# Revit family: IS_Mara_A9009_BIM_NL
name_source: partatom
category: Plumbing Fixtures
revit_build: Autodesk Revit MEP 2014 (Build: 20130308_1515(x64)
units: mm (PartAtom-declared; Revit-internal decimal feet)

## types (1)
- A9009AA - MARA WASTAFELMENGKRAAN HOOG ZONDER WASTE
    AreaUnits = millimeters
    Assembly Code = C1030200
    BIMObjectName = ISI_IdealStandard_WashbasinTaps_A9009AA
    BREEAMApproved = No
    Brand = Ideal Standard
    CWFU = 0
    Cost = 0 $
    Default Elevation = 800 mm  [stored 2.62467 ft]
    ECA = No
    HWFU = 0
    IfcExportAs = IfcValveType
    IfcExportType = Wastafelmengkraan
    LinearUnits = millimeters
    Model = A9009AA
    ModelNumber = A9009AA
    NBSDescription = Water supply fittings for wash basins and troughs
    NBSReference = 45-35-70/371
    Name = WashbasinTaps_A9009AA_IdealStandard
    NominalHeight = 326 mm
    NominalLength = 203 mm
    NominalWidth = 50 mm
    Size = 50 x 203 x 326 mm
    TMV3 = Yes
    TestPressure = 10 Bar
    URL = www.idealstandardnederland.nl
    Uniclass2 = Pr_40_20_87_98
    Uniclass2015Code = Pr_40_20_87_98
    Uniclass2015Description = Washbasin taps
    Uniclass2015Reference = Pr_40_20_87_98
    Uniclass2015Title = Washbasin taps
    Uniclass2015Version = Products v1.1
    Version = 1
    VolumeUnits = liter
    WFU = 0
    WRAS = No
    WarrantyDescription = Fabrieksgarantie
    WarrantyDurationUnit = jaar
    WaterEfficientProduct = No

note: [stored X ft] marks values corroborated as IEEE doubles in the binary element streams (Revit-internal decimal feet)

## geometry (parser evidence)
native form markers: Sweep x1
no freeform markers — native parametric forms only
